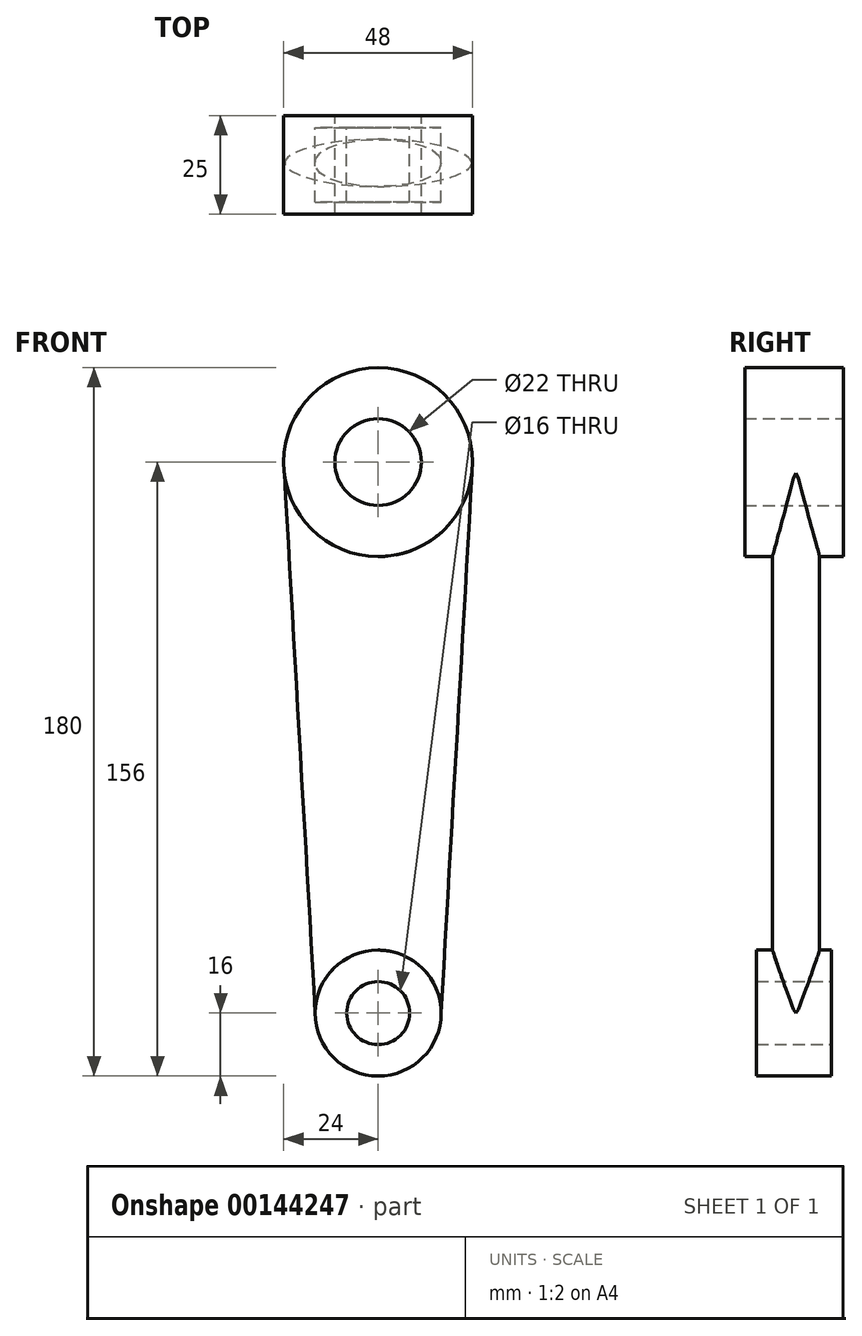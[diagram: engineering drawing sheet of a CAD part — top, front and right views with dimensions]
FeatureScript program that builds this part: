
annotation { "Feature Type Name" : "Feature", "Feature Type Description" : "" }
export const myFeature = defineFeature(function(context is Context, id is Id, definition is map)
    precondition{}
    {
        {
            var Q0;
            Q0=qCreatedBy(makeId("Front.planeOp"),FACE);
            var sketch = newSketch(context, id + "F0", { "sketchPlane" : qUnion([Q0])});
            skCircle(sketch, "E0", {"center": v(0, 140) * mm, "radius": 24 * mm});
            skCircle(sketch, "E1", {"center": v(0, 140) * mm, "radius": 11 * mm});
            skCircle(sketch, "E2", {"center": v(0, 0) * mm, "radius": 8 * mm});
            skCircle(sketch, "E3", {"center": v(0, 0) * mm, "radius": 16 * mm});
            skSolve(sketch);
        }
        {
            var Q0;
            Q0=makeQuery(id+"F0.imprint","IMPRINT",FACE,{"disambiguationData":[TD([[makeQuery(id+"F0.imprint","IMPRINT",EDGE,{"derivedFrom":sQuery(id+"F0.wireOp",EDGE,"E0")}),1.0]])]});
            extrude(context, id + "F1", {"entities" : qUnion([Q0]), "endBound" : BoundingType.SYMMETRIC, "depth" : 25 * mm});
        }
        {
            var Q0;
            Q0=makeQuery(id+"F0.imprint","IMPRINT",FACE,{"disambiguationData":[TD([[makeQuery(id+"F0.imprint","IMPRINT",EDGE,{"derivedFrom":sQuery(id+"F0.wireOp",EDGE,"E2")}),-1.0]])]});
            extrude(context, id + "F2", {"entities" : qUnion([Q0]), "endBound" : BoundingType.SYMMETRIC, "depth" : 19 * mm});
        }
        {
            var Q0;
            Q0=qCreatedBy(makeId("Top.planeOp"),FACE);
            var sketch = newSketch(context, id + "F3", { "sketchPlane" : qUnion([Q0])});
            skEllipse(sketch, "E4", {"center": v(0, 0.5) * mm, "majorRadius": 16 * mm, "minorRadius": 6 * mm, "majorAxis": v(1, 0)});
            skPoint(sketch, "E5", {"position": v(0, 6.5) * mm});
            skLineSegment(sketch, "E6", {"start": v(16, 9.5) * mm, "end": v(16, -9.5) * mm, "construction": true});
            skSolve(sketch);
        }
        {
            var Q0;
            Q0=sQuery(id+"F0.wireOp",VERTEX,"E0.center");
            var Q1;
            Q1=qCreatedBy(makeId("Top.planeOp"),FACE);
            cPlane(context, id + "F4", {"entities" : qUnion([Q0, Q1]), "cplaneType" : CPlaneType.PLANE_POINT, "offset" : 25 * mm, "width" : 150 * mm, "height" : 150 * mm});
        }
        {
            var Q0;
            Q0=qCreatedBy(id+"F4.planeOp",FACE);
            var sketch = newSketch(context, id + "F5", { "sketchPlane" : qUnion([Q0])});
            skEllipse(sketch, "E7", {"center": v(0, 0.5) * mm, "majorRadius": 24 * mm, "minorRadius": 6 * mm, "majorAxis": v(1, 0)});
            skPoint(sketch, "E8", {"position": v(0, 6.5) * mm});
            skLineSegment(sketch, "E9", {"start": v(24, 12.5) * mm, "end": v(24, -12.5) * mm, "construction": true});
            skSolve(sketch);
        }
        {
            var Q0;
            Q0=makeQuery(id+"F5.imprint","IMPRINT",FACE,{"disambiguationData":[TD([[makeQuery(id+"F5.imprint","IMPRINT",EDGE,{"derivedFrom":sQuery(id+"F5.wireOp",EDGE,"E7")}),1.0]])]});
            var Q1;
            Q1=makeQuery(id+"F3.imprint","IMPRINT",FACE,{"disambiguationData":[TD([[makeQuery(id+"F3.imprint","IMPRINT",EDGE,{"derivedFrom":sQuery(id+"F3.wireOp",EDGE,"E4")}),1.0]])]});
            loft(context, id + "F6", {"operationType" : NewBodyOperationType.ADD, "sheetProfilesArray" : [{ "sheetProfileEntities" : qUnion([Q0]) }, { "sheetProfileEntities" : qUnion([Q1]) }]});
        }
        {
            var Q0;
            Q0=makeQuery(id+"F0.imprint","IMPRINT",FACE,{"disambiguationData":[TD([[makeQuery(id+"F0.imprint","IMPRINT",EDGE,{"derivedFrom":sQuery(id+"F0.wireOp",EDGE,"E1")}),1.0]])]});
            extrude(context, id + "F7", {"entities" : qUnion([Q0]), "operationType" : NewBodyOperationType.REMOVE, "endBound" : BoundingType.SYMMETRIC, "oppositeDirection" : true, "depth" : 25 * mm});
        }
        {
            var Q0;
            Q0=makeQuery(id+"F0.imprint","IMPRINT",FACE,{"disambiguationData":[TD([[makeQuery(id+"F0.imprint","IMPRINT",EDGE,{"derivedFrom":sQuery(id+"F0.wireOp",EDGE,"E2")}),1.0]])]});
            extrude(context, id + "F8", {"entities" : qUnion([Q0]), "operationType" : NewBodyOperationType.REMOVE, "endBound" : BoundingType.SYMMETRIC, "depth" : 25 * mm});
        }
    });
